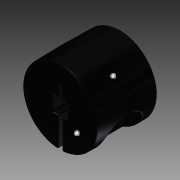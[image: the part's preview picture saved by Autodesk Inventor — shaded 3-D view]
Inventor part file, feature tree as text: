
AUTODESK INVENTOR PART (.ipt)
format: ipt  version: 2015 (Build 190159000, 159)  size: 518,656 bytes
history: native  units: in
note: dims shown in document units (in); Inventor stores cm internally (conversion verified against a paired STEP export)
features: other x2, fillet x1, imported_body x1
ambient origin geometry x8: Origin, YZ Plane, XZ Plane, XY Plane, X Axis, Y Axis, Z Axis, Center Point
bodies: Body1 (feature_tree)
feature tree (4):
  other  "Lock Collar (plastic)"
  fillet  "Fillet3"  [1 undecoded]
  other  "Lock Collar"
  imported_body  "Base1"
note: 1 required parameter value undecoded (feature->parameter linkage not recoverable at this tier; creation-order binding heuristic only, values carry confidence <= 0.55)
